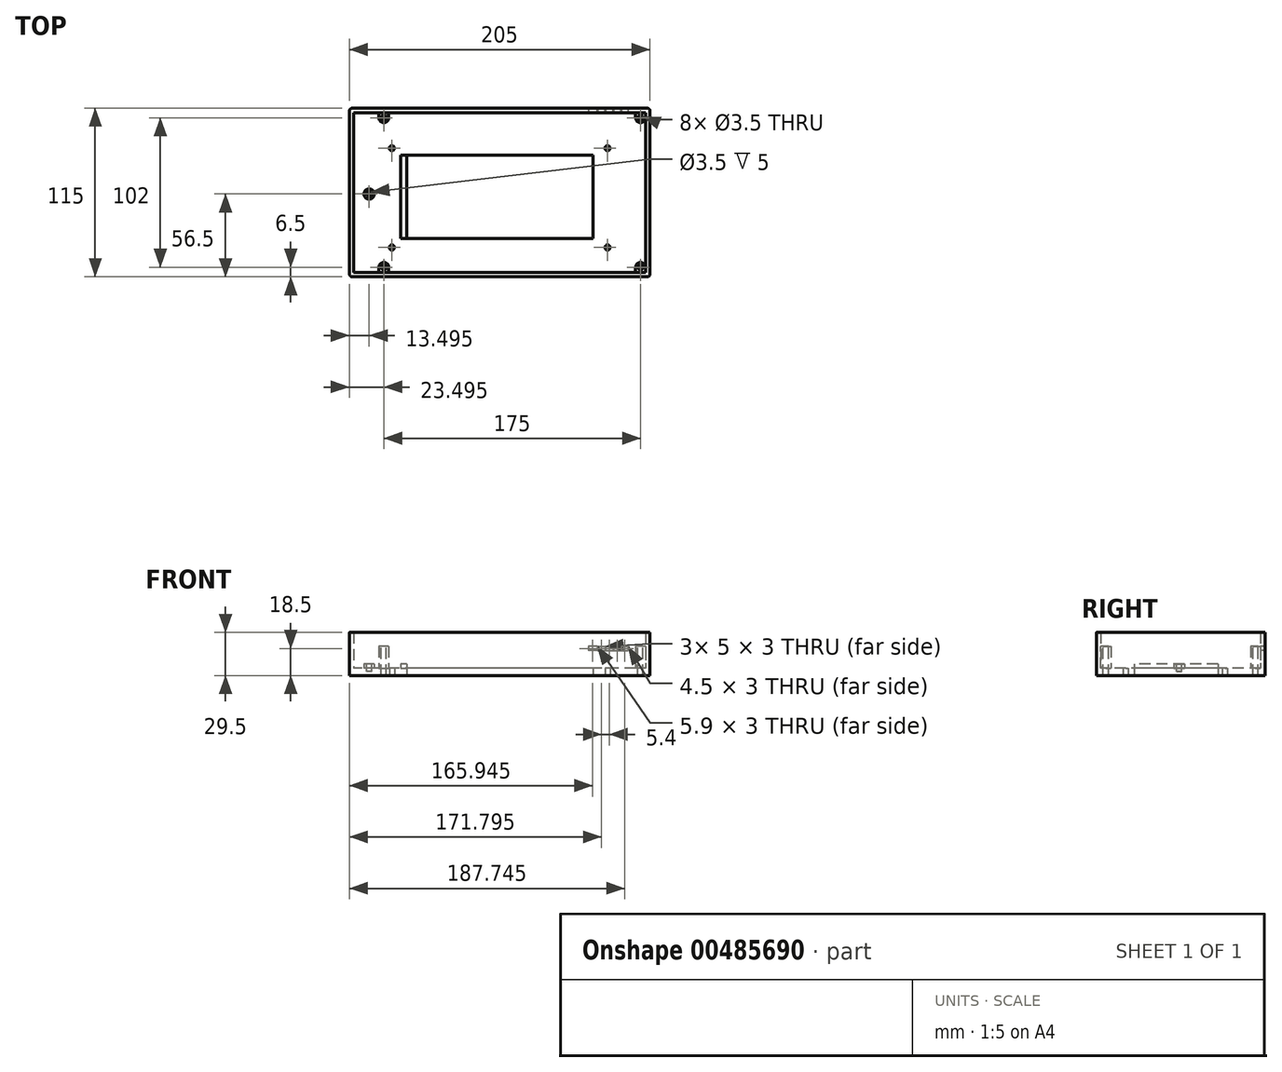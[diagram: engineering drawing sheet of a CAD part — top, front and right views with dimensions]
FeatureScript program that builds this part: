
annotation { "Feature Type Name" : "Feature", "Feature Type Description" : "" }
export const myFeature = defineFeature(function(context is Context, id is Id, definition is map)
    precondition{}
    {
        {
            var Q0;
            Q0=qCreatedBy(makeId("Top.planeOp"),FACE);
            var sketch = newSketch(context, id + "F0", { "sketchPlane" : qUnion([Q0])});
            skLineSegment(sketch, "E0.bottom", {"start": v(-102.37, 35.4) * mm, "end": v(102.63, 35.4) * mm});
            skLineSegment(sketch, "E0.top", {"start": v(-102.37, -79.6) * mm, "end": v(102.63, -79.6) * mm});
            skLineSegment(sketch, "E0.left", {"start": v(-102.37, 35.4) * mm, "end": v(-102.37, -79.6) * mm});
            skLineSegment(sketch, "E0.right", {"start": v(102.63, 35.4) * mm, "end": v(102.63, -79.6) * mm});
            skSolve(sketch);
        }
        {
            var Q0;
            Q0 = qSketchRegion(id + "F0", true);
            extrude(context, id + "F1", {"entities" : qUnion([Q0]), "depth" : 5 * mm});
        }
        {
            var Q0;
            Q0=makeQuery(id+"F1.opExtrude","CAP_FACE",FACE,{"disambiguationData":[OSD([sQuery(id+"F0.wireOp",EDGE,"E0.bottom"),sQuery(id+"F0.wireOp",EDGE,"E0.top"),sQuery(id+"F0.wireOp",EDGE,"E0.left"),sQuery(id+"F0.wireOp",EDGE,"E0.right")])],"isStart":true});
            var sketch = newSketch(context, id + "F2", { "sketchPlane" : qUnion([Q0])});
            skCircle(sketch, "E1", {"center": v(-73.37, 59.6) * mm, "radius": 1.75 * mm});
            skCircle(sketch, "E2", {"center": v(-73.37, -8.14) * mm, "radius": 1.75 * mm});
            skCircle(sketch, "E3", {"center": v(73.63, 59.6) * mm, "radius": 1.75 * mm});
            skCircle(sketch, "E4", {"center": v(73.63, -8.14) * mm, "radius": 1.75 * mm});
            skSolve(sketch);
        }
        {
            var Q0;
            Q0 = qSketchRegion(id + "F2", true);
            extrude(context, id + "F3", {"entities" : qUnion([Q0]), "operationType" : NewBodyOperationType.REMOVE, "oppositeDirection" : true, "depth" : 25 * mm});
        }
        {
            var Q0;
            Q0=makeQuery(id+"F1.opExtrude","CAP_FACE",FACE,{"disambiguationData":[OSD([sQuery(id+"F0.wireOp",EDGE,"E0.bottom"),sQuery(id+"F0.wireOp",EDGE,"E0.top"),sQuery(id+"F0.wireOp",EDGE,"E0.left"),sQuery(id+"F0.wireOp",EDGE,"E0.right")])],"isStart":true});
            var sketch = newSketch(context, id + "F4", { "sketchPlane" : qUnion([Q0])});
            skLineSegment(sketch, "E5.bottom", {"start": v(-63.37, 53.6) * mm, "end": v(63.63, 53.6) * mm});
            skLineSegment(sketch, "E5.top", {"start": v(-63.37, -3.4) * mm, "end": v(63.63, -3.4) * mm});
            skLineSegment(sketch, "E5.left", {"start": v(-63.37, 53.6) * mm, "end": v(-63.37, -3.4) * mm});
            skLineSegment(sketch, "E5.right", {"start": v(63.63, 53.6) * mm, "end": v(63.63, -3.4) * mm});
            skSolve(sketch);
        }
        {
            var Q0;
            Q0=makeQuery(id+"F4.imprint","IMPRINT",FACE,{"disambiguationData":[TD([[makeQuery(id+"F4.imprint","IMPRINT",EDGE,{"derivedFrom":sQuery(id+"F4.wireOp",EDGE,"E5.bottom")}),-1.0]])]});
            extrude(context, id + "F5", {"entities" : qUnion([Q0]), "operationType" : NewBodyOperationType.REMOVE, "oppositeDirection" : true, "depth" : 25 * mm});
        }
        {
            var Q0;
            Q0=makeQuery(id+"F1.opExtrude","CAP_FACE",FACE,{"disambiguationData":[OSD([sQuery(id+"F0.wireOp",EDGE,"E0.bottom"),sQuery(id+"F0.wireOp",EDGE,"E0.top"),sQuery(id+"F0.wireOp",EDGE,"E0.left"),sQuery(id+"F0.wireOp",EDGE,"E0.right")])],"isStart":false});
            var sketch = newSketch(context, id + "F6", { "sketchPlane" : qUnion([Q0])});
            skCircle(sketch, "E6", {"center": v(96.13, -73.1) * mm, "radius": 3.35 * mm});
            skCircle(sketch, "E7", {"center": v(-78.87, -73.1) * mm, "radius": 3.35 * mm});
            skCircle(sketch, "E8", {"center": v(96.13, 28.9) * mm, "radius": 3.35 * mm});
            skCircle(sketch, "E9", {"center": v(-78.87, 28.9) * mm, "radius": 3.35 * mm});
            skLineSegment(sketch, "E10", {"start": v(-75.52, 28.9) * mm, "end": v(-75.52, 35.4) * mm});
            skLineSegment(sketch, "E11", {"start": v(-82.22, 28.9) * mm, "end": v(-82.22, 35.4) * mm});
            skLineSegment(sketch, "E12", {"start": v(96.13, 28.9) * mm, "end": v(92.78, 28.9) * mm});
            skLineSegment(sketch, "E13", {"start": v(92.78, 28.9) * mm, "end": v(92.78, 35.4) * mm});
            skLineSegment(sketch, "E14", {"start": v(96.13, 28.9) * mm, "end": v(99.48, 28.9) * mm});
            skLineSegment(sketch, "E15", {"start": v(99.48, 28.9) * mm, "end": v(99.48, 35.4) * mm});
            skLineSegment(sketch, "E16", {"start": v(96.13, -73.1) * mm, "end": v(92.78, -73.1) * mm});
            skLineSegment(sketch, "E17", {"start": v(92.78, -73.1) * mm, "end": v(92.78, -79.6) * mm});
            skLineSegment(sketch, "E18", {"start": v(96.13, -73.1) * mm, "end": v(99.48, -73.1) * mm});
            skLineSegment(sketch, "E19", {"start": v(99.48, -73.1) * mm, "end": v(99.48, -79.6) * mm});
            skLineSegment(sketch, "E20", {"start": v(-78.87, -73.1) * mm, "end": v(-82.22, -73.1) * mm});
            skLineSegment(sketch, "E21", {"start": v(-82.22, -73.1) * mm, "end": v(-75.52, -73.1) * mm});
            skLineSegment(sketch, "E22", {"start": v(-75.52, -73.1) * mm, "end": v(-75.52, -79.6) * mm});
            skLineSegment(sketch, "E23", {"start": v(-82.22, -73.1) * mm, "end": v(-82.22, -79.6) * mm});
            skSolve(sketch);
        }
        {
            var Q0;
            Q0 = qSketchRegion(id + "F6", true);
            var Q1;
            {var subQ3=sQuery(id+"F6.wireOp",EDGE,"E22");Q1=makeQuery(id+"F6.imprint","IMPRINT",FACE,{"disambiguationData":[TD([[makeQuery(id+"F6.imprint","IMPRINT",EDGE,{"derivedFrom":subQ3}),-1.0]])]});}
            var Q2;
            {var subQ0=sQuery(id+"F6.wireOp",EDGE,"E10");Q2=makeQuery(id+"F6.imprint","IMPRINT",FACE,{"disambiguationData":[TD([[makeQuery(id+"F6.imprint","IMPRINT",EDGE,{"derivedFrom":subQ0}),1.0]])]});}
            var Q3;
            {var subQ0=sQuery(id+"F6.wireOp",EDGE,"E13");Q3=makeQuery(id+"F6.imprint","IMPRINT",FACE,{"disambiguationData":[TD([[makeQuery(id+"F6.imprint","IMPRINT",EDGE,{"derivedFrom":subQ0}),-1.0]])]});}
            var Q4;
            {var subQ0=sQuery(id+"F6.wireOp",EDGE,"E17");Q4=makeQuery(id+"F6.imprint","IMPRINT",FACE,{"disambiguationData":[TD([[makeQuery(id+"F6.imprint","IMPRINT",EDGE,{"derivedFrom":subQ0}),1.0]])]});}
            extrude(context, id + "F7", {"entities" : qUnion([Q0, Q1, Q2, Q3, Q4]), "operationType" : NewBodyOperationType.ADD, "depth" : 15 * mm});
        }
        {
            var Q0;
            Q0=makeQuery(id+"F1.opExtrude","CAP_FACE",FACE,{"disambiguationData":[OSD([sQuery(id+"F0.wireOp",EDGE,"E0.bottom"),sQuery(id+"F0.wireOp",EDGE,"E0.top"),sQuery(id+"F0.wireOp",EDGE,"E0.left"),sQuery(id+"F0.wireOp",EDGE,"E0.right")])],"isStart":false});
            var sketch = newSketch(context, id + "F8", { "sketchPlane" : qUnion([Q0])});
            skLineSegment(sketch, "E24", {"start": v(-78.87, -73.1) * mm, "end": v(-78.87, 28.9) * mm});
            skPoint(sketch, "E25", {"position": v(-78.87, -23.1) * mm});
            skLineSegment(sketch, "E26", {"start": v(-78.87, -23.1) * mm, "end": v(-100.09, -23.1) * mm});
            skCircle(sketch, "E27", {"center": v(-88.87, -23.1) * mm, "radius": 3.5 * mm});
            skSolve(sketch);
        }
        {
            var Q0;
            {var subQ0=sQuery(id+"F8.wireOp",EDGE,"E27");var subQ1=sQuery(id+"F8.wireOp",EDGE,"E26");var subQ2=makeQuery(id+"F8.imprint","INTERSECT",VERTEX,{"disambiguationData":[OD(0.0)],"derivedFrom":[subQ1,subQ0]});Q0=makeQuery(id+"F8.imprint","IMPRINT",FACE,{"disambiguationData":[TD([[makeQuery(id+"F8.imprint","IMPRINT",EDGE,{"disambiguationData":[TD([[subQ2,1.0]])],"derivedFrom":subQ1}),1.0]])]});}
            var Q1;
            {var subQ0=sQuery(id+"F8.wireOp",EDGE,"E27");var subQ1=sQuery(id+"F8.wireOp",EDGE,"E26");var subQ2=makeQuery(id+"F8.imprint","INTERSECT",VERTEX,{"disambiguationData":[OD(0.0)],"derivedFrom":[subQ1,subQ0]});Q1=makeQuery(id+"F8.imprint","IMPRINT",FACE,{"disambiguationData":[TD([[makeQuery(id+"F8.imprint","IMPRINT",EDGE,{"disambiguationData":[TD([[subQ2,1.0]])],"derivedFrom":subQ1}),-1.0]])]});}
            var Q2;
            Q2 = qSketchRegion(id + "F14", true);
            extrude(context, id + "F9", {"entities" : qUnion([Q0, Q1, Q2]), "operationType" : NewBodyOperationType.ADD, "depth" : 3 * mm});
        }
        {
            var Q0;
            Q0=makeQuery(id+"F1.opExtrude","CAP_FACE",FACE,{"disambiguationData":[OSD([sQuery(id+"F0.wireOp",EDGE,"E0.bottom"),sQuery(id+"F0.wireOp",EDGE,"E0.top"),sQuery(id+"F0.wireOp",EDGE,"E0.left"),sQuery(id+"F0.wireOp",EDGE,"E0.right")])],"isStart":false});
            var sketch = newSketch(context, id + "F10", { "sketchPlane" : qUnion([Q0])});
            skLineSegment(sketch, "E28", {"start": v(-63.37, -53.6) * mm, "end": v(-63.37, 3.4) * mm});
            skLineSegment(sketch, "E29", {"start": v(-63.37, 3.4) * mm, "end": v(-67.37, 3.4) * mm});
            skLineSegment(sketch, "E30", {"start": v(-67.37, 3.4) * mm, "end": v(-67.37, -53.6) * mm});
            skLineSegment(sketch, "E31", {"start": v(-67.37, -53.6) * mm, "end": v(-63.37, -53.6) * mm});
            skSolve(sketch);
        }
        {
            var Q0;
            Q0 = qSketchRegion(id + "F10", true);
            extrude(context, id + "F11", {"entities" : qUnion([Q0]), "operationType" : NewBodyOperationType.ADD, "depth" : 3 * mm});
        }
        {
            var Q0;
            Q0=makeQuery(id+"F7.opExtrude","CAP_FACE",FACE,{"disambiguationData":[OSD([sQuery(id+"F6.wireOp",EDGE,"E7")])],"isStart":false});
            var sketch = newSketch(context, id + "F12", { "sketchPlane" : qUnion([Q0])});
            skCircle(sketch, "E32", {"center": v(-78.87, -73.1) * mm, "radius": 1.75 * mm});
            skSolve(sketch);
        }
        {
            var Q0;
            Q0 = qSketchRegion(id + "F12", true);
            extrude(context, id + "F13", {"entities" : qUnion([Q0]), "operationType" : NewBodyOperationType.REMOVE, "oppositeDirection" : true, "depth" : 25 * mm});
        }
        {
            var Q0;
            Q0=makeQuery(id+"F7.opExtrude","CAP_FACE",FACE,{"disambiguationData":[OSD([sQuery(id+"F6.wireOp",EDGE,"E9")])],"isStart":false});
            var sketch = newSketch(context, id + "F14", { "sketchPlane" : qUnion([Q0])});
            skCircle(sketch, "E33", {"center": v(-78.87, 28.9) * mm, "radius": 1.75 * mm});
            skSolve(sketch);
        }
        {
            var Q0;
            Q0 = qSketchRegion(id + "F14", true);
            extrude(context, id + "F15", {"entities" : qUnion([Q0]), "operationType" : NewBodyOperationType.REMOVE, "oppositeDirection" : true, "depth" : 25 * mm});
        }
        {
            var Q0;
            Q0=makeQuery(id+"F7.opExtrude","CAP_FACE",FACE,{"disambiguationData":[OSD([sQuery(id+"F6.wireOp",EDGE,"E6")])],"isStart":false});
            var sketch = newSketch(context, id + "F16", { "sketchPlane" : qUnion([Q0])});
            skCircle(sketch, "E34", {"center": v(96.13, -73.1) * mm, "radius": 1.75 * mm});
            skSolve(sketch);
        }
        {
            var Q0;
            Q0 = qSketchRegion(id + "F16", true);
            extrude(context, id + "F17", {"entities" : qUnion([Q0]), "operationType" : NewBodyOperationType.REMOVE, "oppositeDirection" : true, "depth" : 25 * mm});
        }
        {
            var Q0;
            Q0=makeQuery(id+"F7.opExtrude","CAP_FACE",FACE,{"disambiguationData":[OSD([sQuery(id+"F6.wireOp",EDGE,"E8")])],"isStart":false});
            var sketch = newSketch(context, id + "F18", { "sketchPlane" : qUnion([Q0])});
            skCircle(sketch, "E35", {"center": v(96.13, 28.9) * mm, "radius": 1.75 * mm});
            skSolve(sketch);
        }
        {
            var Q0;
            Q0 = qSketchRegion(id + "F18", true);
            extrude(context, id + "F19", {"entities" : qUnion([Q0]), "operationType" : NewBodyOperationType.REMOVE, "oppositeDirection" : true, "depth" : 25 * mm});
        }
        {
            var Q0;
            Q0=makeQuery(id+"F9.opExtrude","CAP_FACE",FACE,{"disambiguationData":[OSD([sQuery(id+"F8.wireOp",EDGE,"E27")])],"isStart":false});
            var sketch = newSketch(context, id + "F20", { "sketchPlane" : qUnion([Q0])});
            skCircle(sketch, "E36", {"center": v(-88.87, -23.1) * mm, "radius": 1.75 * mm});
            skSolve(sketch);
        }
        {
            var Q0;
            Q0 = qSketchRegion(id + "F20", true);
            extrude(context, id + "F21", {"entities" : qUnion([Q0]), "operationType" : NewBodyOperationType.REMOVE, "oppositeDirection" : true, "depth" : 5 * mm});
        }
        {
            var Q0;
            Q0=makeQuery(id+"F1.opExtrude","CAP_FACE",FACE,{"disambiguationData":[OSD([sQuery(id+"F0.wireOp",EDGE,"E0.bottom"),sQuery(id+"F0.wireOp",EDGE,"E0.top"),sQuery(id+"F0.wireOp",EDGE,"E0.left"),sQuery(id+"F0.wireOp",EDGE,"E0.right")])],"isStart":false});
            var sketch = newSketch(context, id + "F22", { "sketchPlane" : qUnion([Q0])});
            skLineSegment(sketch, "E37", {"start": v(102.63, -79.6) * mm, "end": v(102.63, 35.4) * mm});
            skLineSegment(sketch, "E38", {"start": v(102.63, 35.4) * mm, "end": v(-102.37, 35.4) * mm});
            skLineSegment(sketch, "E39", {"start": v(-102.37, 35.4) * mm, "end": v(-102.37, -79.6) * mm});
            skLineSegment(sketch, "E40", {"start": v(-102.37, -79.6) * mm, "end": v(102.63, -79.6) * mm});
            skLineSegment(sketch, "E41", {"start": v(-99.37, 32.4) * mm, "end": v(-99.37, -76.6) * mm});
            skLineSegment(sketch, "E42", {"start": v(-99.37, -76.6) * mm, "end": v(99.63, -76.6) * mm});
            skLineSegment(sketch, "E43", {"start": v(99.63, -76.6) * mm, "end": v(99.63, 32.4) * mm});
            skLineSegment(sketch, "E44", {"start": v(99.63, 32.4) * mm, "end": v(-99.37, 32.4) * mm});
            skSolve(sketch);
        }
        {
            var Q0;
            Q0=makeQuery(id+"F22.imprint","IMPRINT",FACE,{"disambiguationData":[TD([[makeQuery(id+"F22.imprint","IMPRINT",EDGE,{"derivedFrom":sQuery(id+"F22.wireOp",EDGE,"E37")}),-1.0]])]});
            var Q1;
            {var subQ1=sQuery(id+"F22.wireOp",EDGE,"E39");Q1=makeQuery(id+"F22.imprint","IMPRINT",FACE,{"disambiguationData":[TD([[makeQuery(id+"F22.imprint","IMPRINT",EDGE,{"derivedFrom":subQ1}),1.0]])]});}
            var Q2;
            {var subQ0=sQuery(id+"F22.wireOp",EDGE,"E40");var subQ1=makeQuery(id+"F7.opExtrude","CAP_EDGE",EDGE,{"disambiguationData":[OSD([sQuery(id+"F6.wireOp",EDGE,"E17")])],"isStart":true});var subQ2=makeQuery(id+"F22.imprint","INTERSECT",VERTEX,{"derivedFrom":[subQ1,subQ0]});Q2=makeQuery(id+"F22.imprint","IMPRINT",FACE,{"disambiguationData":[TD([[makeQuery(id+"F22.imprint","IMPRINT",EDGE,{"disambiguationData":[TD([[subQ2,1.0]])],"derivedFrom":subQ0}),1.0]])]});}
            var Q3;
            {var subQ0=sQuery(id+"F22.wireOp",EDGE,"E38");var subQ1=makeQuery(id+"F7.opExtrude","CAP_EDGE",EDGE,{"disambiguationData":[OSD([sQuery(id+"F6.wireOp",EDGE,"E10")])],"isStart":true});var subQ2=makeQuery(id+"F22.imprint","INTERSECT",VERTEX,{"derivedFrom":[subQ1,subQ0]});var subQ3=makeQuery(id+"F7.opExtrude","CAP_EDGE",EDGE,{"disambiguationData":[OSD([sQuery(id+"F6.wireOp",EDGE,"E13")])],"isStart":true});var subQ4=makeQuery(id+"F22.imprint","INTERSECT",VERTEX,{"derivedFrom":[subQ3,subQ0]});Q3=makeQuery(id+"F22.imprint","IMPRINT",FACE,{"disambiguationData":[TD([[makeQuery(id+"F22.imprint","IMPRINT",EDGE,{"disambiguationData":[TD([[subQ2,-1.0],[subQ4,1.0]])],"derivedFrom":subQ0}),-1.0]])]});}
            extrude(context, id + "F23", {"entities" : qUnion([Q0, Q1, Q2, Q3]), "operationType" : NewBodyOperationType.ADD, "depth" : 24.5 * mm});
        }
        {
            var Q0;
            Q0=makeQuery(id+"F23.boolean.opBoolean","MERGE",EDGE,{"derivedFrom":[makeQuery(id+"F1.opExtrude","SWEPT_EDGE",EDGE,{"disambiguationData":[OSD([sQuery(id+"F0.wireOp",EDGE,"E0.top"),sQuery(id+"F0.wireOp",EDGE,"E0.left")])]}),makeQuery(id+"F23.opExtrude","SWEPT_EDGE",EDGE,{"disambiguationData":[OSD([sQuery(id+"F22.wireOp",EDGE,"E39"),sQuery(id+"F22.wireOp",EDGE,"E40")])]})]});
            var Q1;
            Q1=makeQuery(id+"F23.boolean.opBoolean","MERGE",EDGE,{"derivedFrom":[makeQuery(id+"F1.opExtrude","SWEPT_EDGE",EDGE,{"disambiguationData":[OSD([sQuery(id+"F0.wireOp",EDGE,"E0.top"),sQuery(id+"F0.wireOp",EDGE,"E0.right")])]}),makeQuery(id+"F23.opExtrude","SWEPT_EDGE",EDGE,{"disambiguationData":[OSD([sQuery(id+"F22.wireOp",EDGE,"E37"),sQuery(id+"F22.wireOp",EDGE,"E40")])]})]});
            var Q2;
            Q2=makeQuery(id+"F23.boolean.opBoolean","MERGE",EDGE,{"derivedFrom":[makeQuery(id+"F1.opExtrude","SWEPT_EDGE",EDGE,{"disambiguationData":[OSD([sQuery(id+"F0.wireOp",EDGE,"E0.bottom"),sQuery(id+"F0.wireOp",EDGE,"E0.right")])]}),makeQuery(id+"F23.opExtrude","SWEPT_EDGE",EDGE,{"disambiguationData":[OSD([sQuery(id+"F22.wireOp",EDGE,"E37"),sQuery(id+"F22.wireOp",EDGE,"E38")])]})]});
            var Q3;
            Q3=makeQuery(id+"F23.boolean.opBoolean","MERGE",EDGE,{"derivedFrom":[makeQuery(id+"F1.opExtrude","SWEPT_EDGE",EDGE,{"disambiguationData":[OSD([sQuery(id+"F0.wireOp",EDGE,"E0.bottom"),sQuery(id+"F0.wireOp",EDGE,"E0.left")])]}),makeQuery(id+"F23.opExtrude","SWEPT_EDGE",EDGE,{"disambiguationData":[OSD([sQuery(id+"F22.wireOp",EDGE,"E38"),sQuery(id+"F22.wireOp",EDGE,"E39")])]})]});
            fillet(context, id + "F24", {"entities" : qUnion([Q0, Q1, Q2, Q3]), "radius" : 2 * mm, "tangentPropagation" : true, "allowEdgeOverflow" : false});
        }
        {
            var Q0;
            Q0=makeQuery(id+"F23.opExtrude","SWEPT_FACE",FACE,{"disambiguationData":[OSD([sQuery(id+"F22.wireOp",EDGE,"E44")])]});
            var sketch = newSketch(context, id + "F25", { "sketchPlane" : qUnion([Q0])});
            skLineSegment(sketch, "E45.bottom", {"start": v(87.63, 17) * mm, "end": v(60.63, 17) * mm});
            skLineSegment(sketch, "E45.top", {"start": v(87.63, 20) * mm, "end": v(60.63, 20) * mm});
            skLineSegment(sketch, "E45.left", {"start": v(87.63, 17) * mm, "end": v(87.63, 20) * mm});
            skLineSegment(sketch, "E45.right", {"start": v(60.63, 17) * mm, "end": v(60.63, 20) * mm});
            skSolve(sketch);
        }
        {
            var Q0;
            Q0 = qSketchRegion(id + "F25", true);
            extrude(context, id + "F26", {"entities" : qUnion([Q0]), "operationType" : NewBodyOperationType.REMOVE, "oppositeDirection" : true, "depth" : 25 * mm});
        }
        {
            var Q0;
            Q0=makeQuery(id+"F26.boolean.opBoolean","COPY",FACE,{"derivedFrom":makeQuery(id+"F26.opExtrude","SWEPT_FACE",FACE,{"disambiguationData":[OSD([sQuery(id+"F25.wireOp",EDGE,"E45.bottom")])]})});
            var sketch = newSketch(context, id + "F27", { "sketchPlane" : qUnion([Q0])});
            skLineSegment(sketch, "E46", {"start": v(83.13, 35.4) * mm, "end": v(83.13, 32.4) * mm});
            skLineSegment(sketch, "E47", {"start": v(83.13, 32.4) * mm, "end": v(82.73, 32.4) * mm});
            skLineSegment(sketch, "E48", {"start": v(82.73, 32.4) * mm, "end": v(82.73, 35.4) * mm});
            skLineSegment(sketch, "E49", {"start": v(82.73, 35.4) * mm, "end": v(83.13, 35.4) * mm});
            skLineSegment(sketch, "E50", {"start": v(77.73, 35.4) * mm, "end": v(77.73, 32.4) * mm});
            skLineSegment(sketch, "E51", {"start": v(77.73, 32.4) * mm, "end": v(77.33, 32.4) * mm});
            skLineSegment(sketch, "E52", {"start": v(77.33, 32.4) * mm, "end": v(77.33, 35.4) * mm});
            skLineSegment(sketch, "E53", {"start": v(77.33, 35.4) * mm, "end": v(77.73, 35.4) * mm});
            skLineSegment(sketch, "E54", {"start": v(72.33, 35.4) * mm, "end": v(72.33, 32.4) * mm});
            skLineSegment(sketch, "E55", {"start": v(72.33, 32.4) * mm, "end": v(71.93, 32.4) * mm});
            skLineSegment(sketch, "E56", {"start": v(71.93, 32.4) * mm, "end": v(71.93, 35.4) * mm});
            skLineSegment(sketch, "E57", {"start": v(71.93, 35.4) * mm, "end": v(72.33, 35.4) * mm});
            skLineSegment(sketch, "E58", {"start": v(66.93, 35.4) * mm, "end": v(66.93, 32.4) * mm});
            skLineSegment(sketch, "E59", {"start": v(66.93, 32.4) * mm, "end": v(66.53, 32.4) * mm});
            skLineSegment(sketch, "E60", {"start": v(66.53, 32.4) * mm, "end": v(66.53, 35.4) * mm});
            skLineSegment(sketch, "E61", {"start": v(66.53, 35.4) * mm, "end": v(66.93, 35.4) * mm});
            skSolve(sketch);
        }
        {
            var Q0;
            Q0 = qSketchRegion(id + "F27", true);
            extrude(context, id + "F28", {"entities" : qUnion([Q0]), "operationType" : NewBodyOperationType.ADD, "depth" : 3 * mm});
        }
        {
            var Q0;
            Q0=makeQuery(id+"F7.opExtrude","CAP_FACE",FACE,{"disambiguationData":[OSD([sQuery(id+"F0.wireOp",EDGE,"E0.top"),sQuery(id+"F6.wireOp",EDGE,"E7"),sQuery(id+"F6.wireOp",EDGE,"E22"),sQuery(id+"F6.wireOp",EDGE,"E23")])],"isStart":false});
            var sketch = newSketch(context, id + "F29", { "sketchPlane" : qUnion([Q0])});
            skLineSegment(sketch, "E62.bottom", {"start": v(-75.52, -76.6) * mm, "end": v(-82.22, -76.6) * mm});
            skLineSegment(sketch, "E62.top", {"start": v(-75.52, -79.6) * mm, "end": v(-82.22, -79.6) * mm});
            skLineSegment(sketch, "E62.left", {"start": v(-75.52, -76.6) * mm, "end": v(-75.52, -79.6) * mm});
            skLineSegment(sketch, "E62.right", {"start": v(-82.22, -76.6) * mm, "end": v(-82.22, -79.6) * mm});
            skSolve(sketch);
        }
        {
            var Q0;
            Q0 = qSketchRegion(id + "F29", true);
            extrude(context, id + "F30", {"entities" : qUnion([Q0]), "operationType" : NewBodyOperationType.ADD, "depth" : 9.5 * mm});
        }
        {
            var Q0;
            Q0=makeQuery(id+"F7.opExtrude","CAP_FACE",FACE,{"disambiguationData":[OSD([sQuery(id+"F0.wireOp",EDGE,"E0.top"),sQuery(id+"F6.wireOp",EDGE,"E6"),sQuery(id+"F6.wireOp",EDGE,"E17"),sQuery(id+"F6.wireOp",EDGE,"E19")])],"isStart":false});
            var sketch = newSketch(context, id + "F31", { "sketchPlane" : qUnion([Q0])});
            skLineSegment(sketch, "E63.bottom", {"start": v(92.78, -79.6) * mm, "end": v(99.48, -79.6) * mm});
            skLineSegment(sketch, "E63.top", {"start": v(92.78, -76.6) * mm, "end": v(99.48, -76.6) * mm});
            skLineSegment(sketch, "E63.left", {"start": v(92.78, -79.6) * mm, "end": v(92.78, -76.6) * mm});
            skLineSegment(sketch, "E63.right", {"start": v(99.48, -79.6) * mm, "end": v(99.48, -76.6) * mm});
            skSolve(sketch);
        }
        {
            var Q0;
            Q0 = qSketchRegion(id + "F31", true);
            extrude(context, id + "F32", {"entities" : qUnion([Q0]), "operationType" : NewBodyOperationType.ADD, "depth" : 9.5 * mm});
        }
        {
            var Q0;
            Q0=makeQuery(id+"F7.opExtrude","CAP_FACE",FACE,{"disambiguationData":[OSD([sQuery(id+"F0.wireOp",EDGE,"E0.bottom"),sQuery(id+"F6.wireOp",EDGE,"E8"),sQuery(id+"F6.wireOp",EDGE,"E13"),sQuery(id+"F6.wireOp",EDGE,"E15")])],"isStart":false});
            var sketch = newSketch(context, id + "F33", { "sketchPlane" : qUnion([Q0])});
            skLineSegment(sketch, "E64.bottom", {"start": v(92.78, 32.4) * mm, "end": v(99.48, 32.4) * mm});
            skLineSegment(sketch, "E64.top", {"start": v(92.78, 35.4) * mm, "end": v(99.48, 35.4) * mm});
            skLineSegment(sketch, "E64.left", {"start": v(92.78, 32.4) * mm, "end": v(92.78, 35.4) * mm});
            skLineSegment(sketch, "E64.right", {"start": v(99.48, 32.4) * mm, "end": v(99.48, 35.4) * mm});
            skSolve(sketch);
        }
        {
            var Q0;
            Q0 = qSketchRegion(id + "F33", true);
            extrude(context, id + "F34", {"entities" : qUnion([Q0]), "operationType" : NewBodyOperationType.ADD, "depth" : 9.5 * mm});
        }
        {
            var Q0;
            Q0=makeQuery(id+"F7.opExtrude","CAP_FACE",FACE,{"disambiguationData":[OSD([sQuery(id+"F0.wireOp",EDGE,"E0.bottom"),sQuery(id+"F6.wireOp",EDGE,"E9"),sQuery(id+"F6.wireOp",EDGE,"E10"),sQuery(id+"F6.wireOp",EDGE,"E11")])],"isStart":false});
            var sketch = newSketch(context, id + "F35", { "sketchPlane" : qUnion([Q0])});
            skLineSegment(sketch, "E65.bottom", {"start": v(-82.22, 32.4) * mm, "end": v(-75.52, 32.4) * mm});
            skLineSegment(sketch, "E65.top", {"start": v(-82.22, 35.4) * mm, "end": v(-75.52, 35.4) * mm});
            skLineSegment(sketch, "E65.left", {"start": v(-82.22, 32.4) * mm, "end": v(-82.22, 35.4) * mm});
            skLineSegment(sketch, "E65.right", {"start": v(-75.52, 32.4) * mm, "end": v(-75.52, 35.4) * mm});
            skSolve(sketch);
        }
        {
            var Q0;
            Q0 = qSketchRegion(id + "F35", true);
            extrude(context, id + "F36", {"entities" : qUnion([Q0]), "operationType" : NewBodyOperationType.ADD, "depth" : 9.5 * mm});
        }
    });
